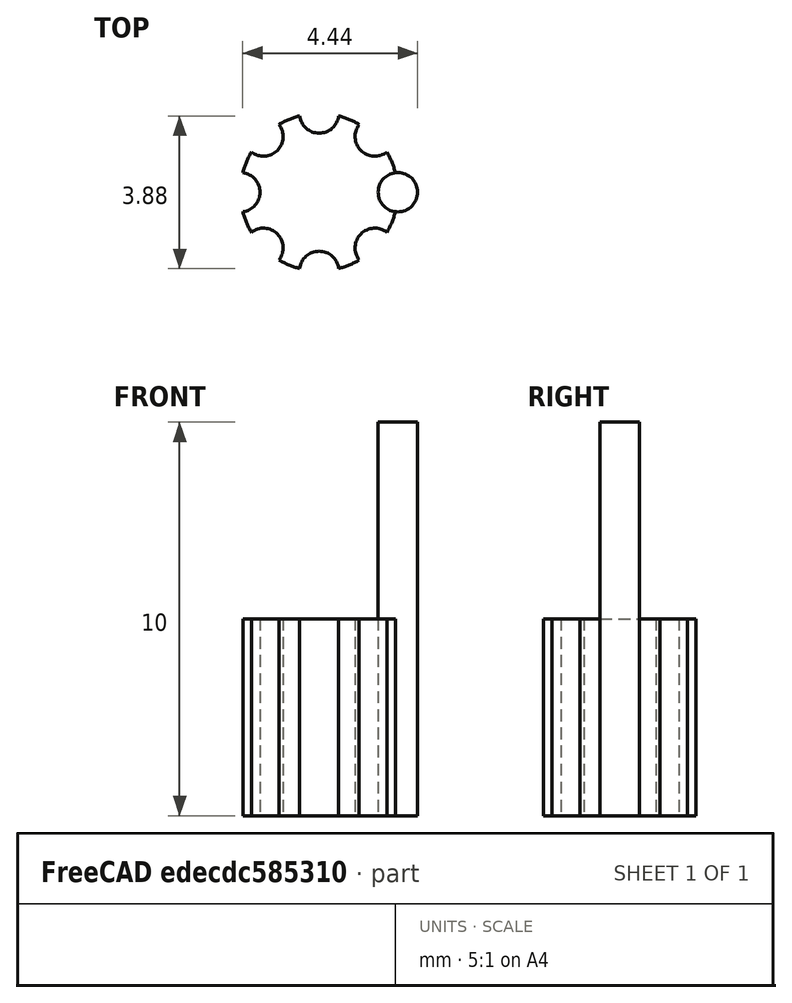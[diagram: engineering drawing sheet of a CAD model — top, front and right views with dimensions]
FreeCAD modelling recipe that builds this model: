
FCSTD DOCUMENT  (FreeCAD 0.20R29177 (Git))
Label: Ejercicio1Video11
License: All rights reserved
LicenseURL: http://en.wikipedia.org/wiki/All_rights_reserved
objects: Part::Cylinder×2, Part::FeaturePython×1, Part::Cut×1
note: 3 computed .brp shape members not serialized (recipe doc carries the construction recipe); baked Part::Feature solids carry a one-line shape summary decoded from their .brp

FEATURE [Part::Cylinder] Cylinder  label="Cilindro_base"
  Angle = 360
  AttacherType = Attacher::AttachEngine3D
  FirstAngle = 0
  Height = 5
  Radius = 2
  SecondAngle = 0
FEATURE [Part::Cylinder] Cylinder001  label="Cilindro_master"
  Angle = 360
  AttacherType = Attacher::AttachEngine3D
  FirstAngle = 0
  Height = 10
  Placement = pos=(2,0,0) rot=(0.57735,0.57735,0.57735;0rad)
  Radius = 0.5
  SecondAngle = 0
FEATURE [Part::FeaturePython] Array  # Draft array (typed FeaturePython)
  AlwaysSyncPlacement = false
  Angle = 360
  ArrayType = 1
  Axis = (0,0,1)
  Base = -> Cylinder001
  Center = (0,0,0)
  Count = 8
  ExpandArray = false
  Fuse = false
  IntervalAxis = (0,0,0)
  IntervalX = (100,0,0)
  IntervalY = (0,100,0)
  IntervalZ = (0,0,100)
  NumberCircles = 3
  NumberPolar = 8
  NumberX = 2
  NumberY = 2
  NumberZ = 1
  PlacementList = 8 placements: [(2,0,0),(1.41421,1.41421,0),(4.44089e-16,2,0),(-1.41421,1.41421,0),(-2,2.44929e-16,0),(-1.41421,-1.41421,0),(-4.44089e-16,-2,0),(1.41421,-1.41421,0)]
  RadialDistance = 50
  ScaleList = (8) [(1,1,1),(1,1,1),(1,1,1),(1,1,1),(1,1,1),(1,1,1),(1,1,1),(1,1,1)]
  Symmetry = 1
  TangentialDistance = 25
FEATURE [Part::Cut] Cut
  Base = -> Cylinder
  Tool = -> Array
